# Revit family: 02572103
name_source: partatom
category: Plumbing Fixtures
revit_build: Autodesk Revit 2016 (Build: 20150220_1215(x64)
units: mm (PartAtom-declared; Revit-internal decimal feet)

## family parameters
Always vertical = Yes
Cut with Voids When Loaded = No
OmniClass Number = 23.45.55.00
OmniClass Title = Sanitary Faucets, Wastes
Part Type = Normal
Room Calculation Point = No
Round Connector Dimension = Use Diameter
Shared = No
Work Plane-Based = No

## types (1)
- 02572103 Washbasin and kitchen faucet
    2D/3D/BIM Files URL = http://static.hansa.com
    Advanced Features = DZR brass;Low lead <0.3;Waterways without nickel coating;
    Aerator = Laminar, HONEYCOMB®
    Approval ABP = PA-IX 28473/IA
    Approval DVGW = NW-6506CR0028
    AssetType = Fixed
    BIMObjectName = 02572103
    BodyMaterial = Brass
    Brand = Hansa
    Catalog Drawing URL = http://static.hansa.com
    Category = Health & Care
    CloseOffRating = 0
    Color = Chrome
    Comfort Sales Argument = Quick and easy to clean.
    Connection = Covered eccentric unions
    ConvergoRefNr = 0087-1803-0035-FI
    Customs Code = 84818011
    DN Size = DN15
    DurationUnit = Year
    EAN Number = 4015474267268
    FDV Document URL = http://www.hansa.com
    FaucetMainMaterial = Brass
    Features = Single lever
    Finish = Polished
    Flow = Laminar flow
    Flow Drawing URL = http://static.hansa.com
    Flow Rate At 300kPa = 0.2 L/s
    FlowCoefficient = 0
    Group = Washbasin faucets
    Health Sales Arguments = Brass in contact with drinking water contains less than 0.3% lead.;Surfaces in contact with drinking water do not have a nickel coating.
    IfcExportAs = IfcValveType
    IfcExportType = FAUCET
    Installation Type = Wall-mounted
    Installation Width = cc150 ± 10 mm
    Installation and Maintenance = http://static.hansa.com
    Lever Handle = Lever with H+C symbol
    Long Marketing = Wall-mounted washbasin faucet. Firm long lever offers good usability to all users and situations. Spout 226 mm with laminar flow.  Swivel range 120°  (delivery status) or lockable in middle position. Spout projection 311 mm. Includes eccentric connections.
    ManufacterURL = http://www.hansa.com
    Manufacturer = Hansa
    ManufacturerName = Hansa
    Market = AUT;BEL;CZE;DEU;ESP;INT;ITA;NLD;SVK
    Material = Brass
    Model = 02572103 Washbasin and kitchen faucet
    ModelReference = 02572103
    Mounting Holes = 2 mounting holes
    NBSDescription = Water supply fittings for wash basin and troughs
    NBSReference = 45-35-70/370
    Name = 02572103 Washbasin and kitchen faucet
    Name_en = 02572103 Washbasin and kitchen faucet
    NominalDepth = 326 mm
    NominalHeight = 201 mm
    NominalWidth = 215 mm
    Package Weight = 3.58 kg
    Package external Dimensions = 345 x 218 x 202
    Product Code = 02572103
    Product Datasheet = http://www.hansa.com
    Product Family = HANSAMEDIPRO
    Product Image URL = http://static.hansa.com
    Product URL = http://static.hansa.com
    Projection = 311 mm
    Revision = 2
    Shape = Sculptured
    Size = 215x325.5x201 mm
    Spare Parts = http://static.hansa.com
    Spout Swivel Range = 120°
    Spout Type = Swivel spout
    URL ABP = http://static.hansa.com
    URL DVGW = http://static.hansa.com
    Uniclass2 = Pr_40_30_96_96
    Uniclass2015Description = Washbasin manual water supply sets
    Uniclass2015Reference = Pr_40_20_87_96
    Usage Group = Toilets for the Disabled;Pharmacies, Opticians, Dentists;Health centers & Child welfare clinics;Hospitals
    Version = 2
    VersionDate = 01/01/2019
    WarrantyDescription = http://warranty.hansa.com
    WarrantyDurationUnit = Year

## geometry (parser evidence)
native form markers: Sweep x4
no freeform markers — native parametric forms only
